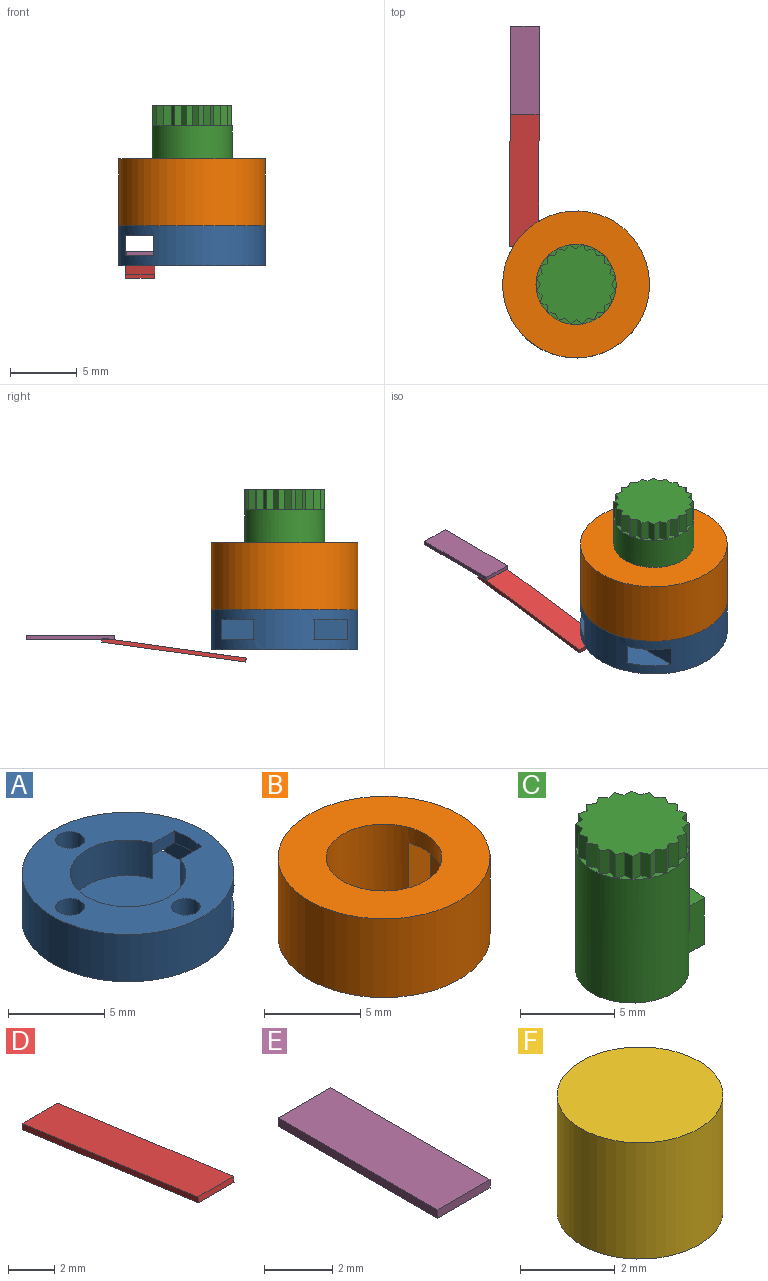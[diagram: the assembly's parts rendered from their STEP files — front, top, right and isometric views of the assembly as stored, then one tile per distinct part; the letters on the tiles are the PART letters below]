
ASSEMBLY  parts=6 mates=6
PART A: 15 faces, bbox 11x11x3 mm
  f0: plane 1.56x0.75mm, normal (0,1,0), area 1.2mm2, adj f1,f4,f5,f12
  f1: cylinder r=4.5mm len=2mm, axis (0,0,1), area 1.5mm2, adj f0,f2,f5,f12
  f2: plane 1.56x0.75mm, normal (0,-1,0), area 1.2mm2, adj f1,f4,f5,f12
  f3: cylinder r=5.5mm len=11mm, axis (0,0,1), area 93.8mm2, adj f5,f6,f10,f11,f12,f13,f14
  f4: cylinder r=3mm len=6mm, axis (0,0,1), area 37.8mm2, adj f0,f2,f5,f10,f11,f13
  f5: plane 11x11mm, normal (0,0,1), area 58.4mm2, adj f0,f1,f2,f3,f4,f7,f8,f9
  f6: plane 11x11mm, normal (0,0,-1), area 89.7mm2, adj f3,f7,f8,f9
  f7: cylinder r=0.75mm len=3mm, axis (0,0,-1), area 14.1mm2, adj f5,f6
  f8: cylinder r=0.75mm len=3mm, axis (0,0,-1), area 14.1mm2, adj f5,f6
  f9: cylinder r=0.75mm len=3mm, axis (0,0,-1), area 14.1mm2, adj f5,f6
  f10: plane 3.72x1.5mm, normal (1,0,0), area 5.6mm2, adj f3,f4,f12,f13
  f11: plane 3.72x1.5mm, normal (1,0,0), area 5.6mm2, adj f3,f4,f12,f13
  f12: plane 9.43x2.17mm, normal (0,0,-1), area 13mm2, adj f0,f1,f2,f3,f10,f11,f14
  f13: plane 9.43x8mm, normal (0,0,1), area 44.3mm2, adj f3,f4,f10,f11,f14
  f14: plane 4.58x1.5mm, normal (-1,0,0), area 6.9mm2, adj f3,f12,f13
PART B: 17 faces, bbox 11x11x5 mm
  f0: cylinder r=4.5mm len=5.39mm, axis (0,0,-1), area 23.4mm2, adj f1,f4,f6,f7,f8,f9,f10
  f1: plane 5.39x3.5mm, normal (0,0,-1), area 8.8mm2, adj f0,f5,f8,f9
  f2: cylinder r=5.5mm len=11mm, axis (0,0,-1), area 172.8mm2, adj f3,f4
  f3: plane 11x11mm, normal (0,0,1), area 66.8mm2, adj f2,f5
  f4: plane 11x11mm, normal (0,0,-1), area 58.4mm2, adj f0,f2,f5,f7,f8,f11,f13,f15
  f5: cylinder r=3mm len=6mm, axis (0,0,1), area 77.9mm2, adj f1,f3,f4,f6,f7,f8,f9,f10
  f6: plane 3.24x2.89mm, normal (0,0,1), area 5mm2, adj f0,f5,f9,f10
  f7: plane 1.56x0.5mm, normal (0,1,0), area 0.8mm2, adj f0,f4,f5,f10
  f8: plane 4x1.56mm, normal (0,-1,0), area 6.2mm2, adj f0,f1,f4,f5
  f9: plane 3x1.56mm, normal (1,0,0), area 4.7mm2, adj f0,f1,f5,f6
  f10: plane 1.8x0.51mm, normal (0,0.71,0.71), area 1.1mm2, adj f0,f5,f6,f7
  f11: cylinder r=0.75mm len=4.25mm, axis (0,0,-1), area 20mm2, adj f4,f12
  f12: plane 1.5x1.5mm, normal (0,0,-1), area 1.8mm2, adj f11
  f13: cylinder r=0.75mm len=4.25mm, axis (0,0,-1), area 20mm2, adj f4,f14
  f14: plane 1.5x1.5mm, normal (0,0,-1), area 1.8mm2, adj f13
  f15: cylinder r=0.75mm len=4.25mm, axis (0,0,-1), area 20mm2, adj f4,f16
  f16: plane 1.5x1.5mm, normal (0,0,-1), area 1.8mm2, adj f15
PART C: 69 faces, bbox 7.5x6x9.5 mm
  f0: cylinder r=3mm len=8mm, axis (0,0,-1), area 144.7mm2, adj f2,f3,f4,f5,f6,f7,f8,f9
  f1: cylinder r=4.5mm len=3mm, axis (0,0,-1), area 6.1mm2, adj f2,f3,f4,f5
  f2: plane 3x1.56mm, normal (0,-1,0), area 4.7mm2, adj f0,f1,f4,f5
  f3: plane 3x1.56mm, normal (0,1,0), area 4.7mm2, adj f0,f1,f4,f5
  f4: plane 2x1.67mm, normal (0,0,1), area 3mm2, adj f0,f1,f2,f3
  f5: plane 7.5x6mm, normal (0,0,-1), area 21.7mm2, adj f0,f1,f2,f3,f67
  f6: plane 0.89x0.43mm, normal (0,0,1), area 0.2mm2, adj f0,f26,f65
  f7: plane 0.75x0.56mm, normal (0,0,1), area 0.2mm2, adj f0,f63,f64
  f8: plane 0.77x0.54mm, normal (0,0,1), area 0.2mm2, adj f0,f61,f62
  f9: plane 0.9x0.43mm, normal (0,0,1), area 0.2mm2, adj f0,f59,f60
  f10: plane 0.94x0.34mm, normal (0,0,1), area 0.2mm2, adj f0,f57,f58
  f11: plane 0.89x0.43mm, normal (0,0,1), area 0.2mm2, adj f0,f55,f56
  f12: plane 0.75x0.56mm, normal (0,0,1), area 0.2mm2, adj f0,f53,f54
  f13: plane 0.77x0.54mm, normal (0,0,1), area 0.2mm2, adj f0,f51,f52
  f14: plane 0.9x0.43mm, normal (0,0,1), area 0.2mm2, adj f0,f49,f50
  f15: plane 0.94x0.34mm, normal (0,0,1), area 0.2mm2, adj f0,f47,f48
  f16: plane 0.89x0.43mm, normal (0,0,1), area 0.2mm2, adj f0,f45,f46
  f17: plane 0.75x0.56mm, normal (0,0,1), area 0.2mm2, adj f0,f43,f44
  f18: plane 0.77x0.54mm, normal (0,0,1), area 0.2mm2, adj f0,f41,f42
  f19: plane 0.9x0.43mm, normal (0,0,1), area 0.2mm2, adj f0,f39,f40
  f20: plane 0.94x0.34mm, normal (0,0,1), area 0.2mm2, adj f0,f37,f38
  f21: plane 0.89x0.43mm, normal (0,0,1), area 0.2mm2, adj f0,f35,f36
  f22: plane 0.75x0.56mm, normal (0,0,1), area 0.2mm2, adj f0,f33,f34
  f23: plane 0.77x0.54mm, normal (0,0,1), area 0.2mm2, adj f0,f31,f32
  f24: plane 0.9x0.43mm, normal (0,0,1), area 0.2mm2, adj f0,f29,f30
  f25: plane 0.94x0.34mm, normal (0,0,1), area 0.2mm2, adj f0,f27,f28
  f26: plane 1.5x0.43mm, normal (0.63,0.78,0), area 0.8mm2, adj f6,f27,f65,f66
  f27: plane 1.5x0.47mm, normal (0.85,-0.53,0), area 0.8mm2, adj f25,f26,f28,f66
  f28: plane 1.5x0.47mm, normal (0.84,0.54,0), area 0.8mm2, adj f25,f27,f29,f66
  f29: plane 1.5x0.43mm, normal (0.64,-0.76,0), area 0.8mm2, adj f24,f28,f30,f66
  f30: plane 1.5x0.54mm, normal (0.97,0.26,0), area 0.8mm2, adj f24,f29,f31,f66
  f31: plane 1.5x0.52mm, normal (0.38,-0.93,0), area 0.8mm2, adj f23,f30,f32,f66
  f32: plane 1.5x0.56mm, normal (1,-0.05,0), area 0.8mm2, adj f23,f31,f33,f66
  f33: plane 1.5x0.55mm, normal (0.07,-1,0), area 0.8mm2, adj f22,f32,f34,f66
  f34: plane 1.5x0.52mm, normal (0.93,-0.36,0), area 0.8mm2, adj f22,f33,f35,f66
  f35: plane 1.5x0.54mm, normal (-0.24,-0.97,0), area 0.8mm2, adj f21,f34,f36,f66
  f36: plane 1.5x0.43mm, normal (0.78,-0.63,0), area 0.8mm2, adj f21,f35,f37,f66
  f37: plane 1.5x0.47mm, normal (-0.53,-0.85,0), area 0.8mm2, adj f20,f36,f38,f66
  f38: plane 1.5x0.47mm, normal (0.54,-0.84,0), area 0.8mm2, adj f20,f37,f39,f66
  f39: plane 1.5x0.43mm, normal (-0.76,-0.64,0), area 0.8mm2, adj f19,f38,f40,f66
  f40: plane 1.5x0.54mm, normal (0.26,-0.97,0), area 0.8mm2, adj f19,f39,f41,f66
  f41: plane 1.5x0.52mm, normal (-0.93,-0.38,0), area 0.8mm2, adj f18,f40,f42,f66
  f42: plane 1.5x0.56mm, normal (-0.05,-1,0), area 0.8mm2, adj f18,f41,f43,f66
  f43: plane 1.5x0.55mm, normal (-1,-0.07,0), area 0.8mm2, adj f17,f42,f44,f66
  f44: plane 1.5x0.52mm, normal (-0.36,-0.93,0), area 0.8mm2, adj f17,f43,f45,f66
  f45: plane 1.5x0.54mm, normal (-0.97,0.24,0), area 0.8mm2, adj f16,f44,f46,f66
  f46: plane 1.5x0.43mm, normal (-0.63,-0.78,0), area 0.8mm2, adj f16,f45,f47,f66
  f47: plane 1.5x0.47mm, normal (-0.85,0.53,0), area 0.8mm2, adj f15,f46,f48,f66
  f48: plane 1.5x0.47mm, normal (-0.84,-0.54,0), area 0.8mm2, adj f15,f47,f49,f66
  f49: plane 1.5x0.43mm, normal (-0.64,0.76,0), area 0.8mm2, adj f14,f48,f50,f66
  f50: plane 1.5x0.54mm, normal (-0.97,-0.26,0), area 0.8mm2, adj f14,f49,f51,f66
  f51: plane 1.5x0.52mm, normal (-0.38,0.93,0), area 0.8mm2, adj f13,f50,f52,f66
  f52: plane 1.5x0.56mm, normal (-1,0.05,0), area 0.8mm2, adj f13,f51,f53,f66
  f53: plane 1.5x0.55mm, normal (-0.07,1,0), area 0.8mm2, adj f12,f52,f54,f66
  f54: plane 1.5x0.52mm, normal (-0.93,0.36,0), area 0.8mm2, adj f12,f53,f55,f66
  f55: plane 1.5x0.54mm, normal (0.24,0.97,0), area 0.8mm2, adj f11,f54,f56,f66
  f56: plane 1.5x0.43mm, normal (-0.78,0.63,0), area 0.8mm2, adj f11,f55,f57,f66
  f57: plane 1.5x0.47mm, normal (0.53,0.85,0), area 0.8mm2, adj f10,f56,f58,f66
  f58: plane 1.5x0.47mm, normal (-0.54,0.84,0), area 0.8mm2, adj f10,f57,f59,f66
  f59: plane 1.5x0.43mm, normal (0.76,0.64,0), area 0.8mm2, adj f9,f58,f60,f66
  f60: plane 1.5x0.54mm, normal (-0.26,0.97,0), area 0.8mm2, adj f9,f59,f61,f66
  f61: plane 1.5x0.52mm, normal (0.93,0.38,0), area 0.8mm2, adj f8,f60,f62,f66
  f62: plane 1.5x0.56mm, normal (0.05,1,0), area 0.8mm2, adj f8,f61,f63,f66
  f63: plane 1.5x0.55mm, normal (1,0.07,0), area 0.8mm2, adj f7,f62,f64,f66
  f64: plane 1.5x0.52mm, normal (0.36,0.93,0), area 0.8mm2, adj f7,f63,f65,f66
  f65: plane 1.5x0.54mm, normal (0.97,-0.24,0), area 0.8mm2, adj f6,f26,f64,f66
  f66: plane 5.94x5.94mm, normal (0,0,1), area 25mm2, adj f26,f27,f28,f29,f30,f31,f32,f33
  f67: cylinder r=1.75mm len=3.5mm, axis (0,0,-1), area 33mm2, adj f5,f68
  f68: plane 3.5x3.5mm, normal (0,0,-1), area 9.6mm2, adj f67
PART D: 6 faces, bbox 2.2x10.8x1.8 mm
  f0: plane 10.82x1.8mm, normal (1,0,0), area 3.3mm2, adj f1,f2,f3,f4
  f1: plane 2.17x0.3mm, normal (0,-0.99,0.14), area 0.7mm2, adj f0,f2,f4,f5
  f2: plane 10.78x2.17mm, normal (0,-0.14,-0.99), area 23.6mm2, adj f0,f1,f3,f5
  f3: plane 2.17x0.3mm, normal (0,0.99,-0.14), area 0.7mm2, adj f0,f2,f4,f5
  f4: plane 10.78x2.17mm, normal (0,0.14,0.99), area 23.6mm2, adj f0,f1,f3,f5
  f5: plane 10.82x1.8mm, normal (-1,0,0), area 3.3mm2, adj f1,f2,f3,f4
PART E: 6 faces, bbox 2.2x6.6x0.3 mm
  f0: plane 6.6x0.3mm, normal (1,0,0), area 2mm2, adj f1,f3,f4,f5
  f1: plane 6.6x2.17mm, normal (0,0,-1), area 14.3mm2, adj f0,f2,f3,f4
  f2: plane 6.6x0.3mm, normal (-1,0,0), area 2mm2, adj f1,f3,f4,f5
  f3: plane 2.17x0.3mm, normal (0,1,0), area 0.7mm2, adj f0,f1,f2,f5
  f4: plane 2.17x0.3mm, normal (0,-1,0), area 0.7mm2, adj f0,f1,f2,f5
  f5: plane 6.6x2.17mm, normal (0,0,1), area 14.3mm2, adj f0,f2,f3,f4
PART F: 5 faces, bbox 3.5x3.5x3 mm
  f0: plane 3.5x3.5mm, normal (0,0,-1), area 4.7mm2, adj f1,f2
  f1: cylinder r=1.25mm len=2.5mm, axis (0,0,1), area 15.7mm2, adj f0,f4
  f2: cylinder r=1.75mm len=3.5mm, axis (0,0,1), area 33mm2, adj f0,f3
  f3: plane 3.5x3.5mm, normal (0,0,1), area 9.6mm2, adj f2
  f4: plane 2.5x2.5mm, normal (0,0,-1), area 4.9mm2, adj f1
PLACE A rot(axis=(0,0,1),179.7deg) t=(-5.49,-1,2.04)mm
PLACE B rot(axis=(0,0,1),179.7deg) t=(-5.49,-1,2.04)mm fixed
PLACE C rot(axis=(0,0,1),179.7deg) t=(-5.49,-1,1.5)mm
PLACE D rot(axis=(0,0,1),179.7deg) t=(-5.43,11.64,0.66)mm
PLACE E rot(axis=(0,0,-1),0.3deg) t=(-13.22,18.59,2.04)mm
PLACE F rot(axis=(0,0,1),153.2deg) t=(-5.49,-1,1.5)mm
MATE planar B.f4 <-> A.f5  axis (0,0,-1) through (-5.43,-1,2.04)mm
MATE planar D.f5 <-> A.f10  axis (1,0,0) through (-8.28,7.28,-0.99)mm
MATE planar F.f2 <-> C.f67  axis (0,0,1) through (-5.49,-1,4.5)mm
MATE slider C.f0 <-> B.f5  axis (0,0,-1) through (-5.49,-1,5.5)mm
MATE planar E.f1 <-> A.f13  axis (0,0,-1) through (-9.33,15.06,-0.21)mm
MATE planar E.f0 <-> A.f11  axis (1,0,0) through (-8.24,15.06,-0.06)mm
